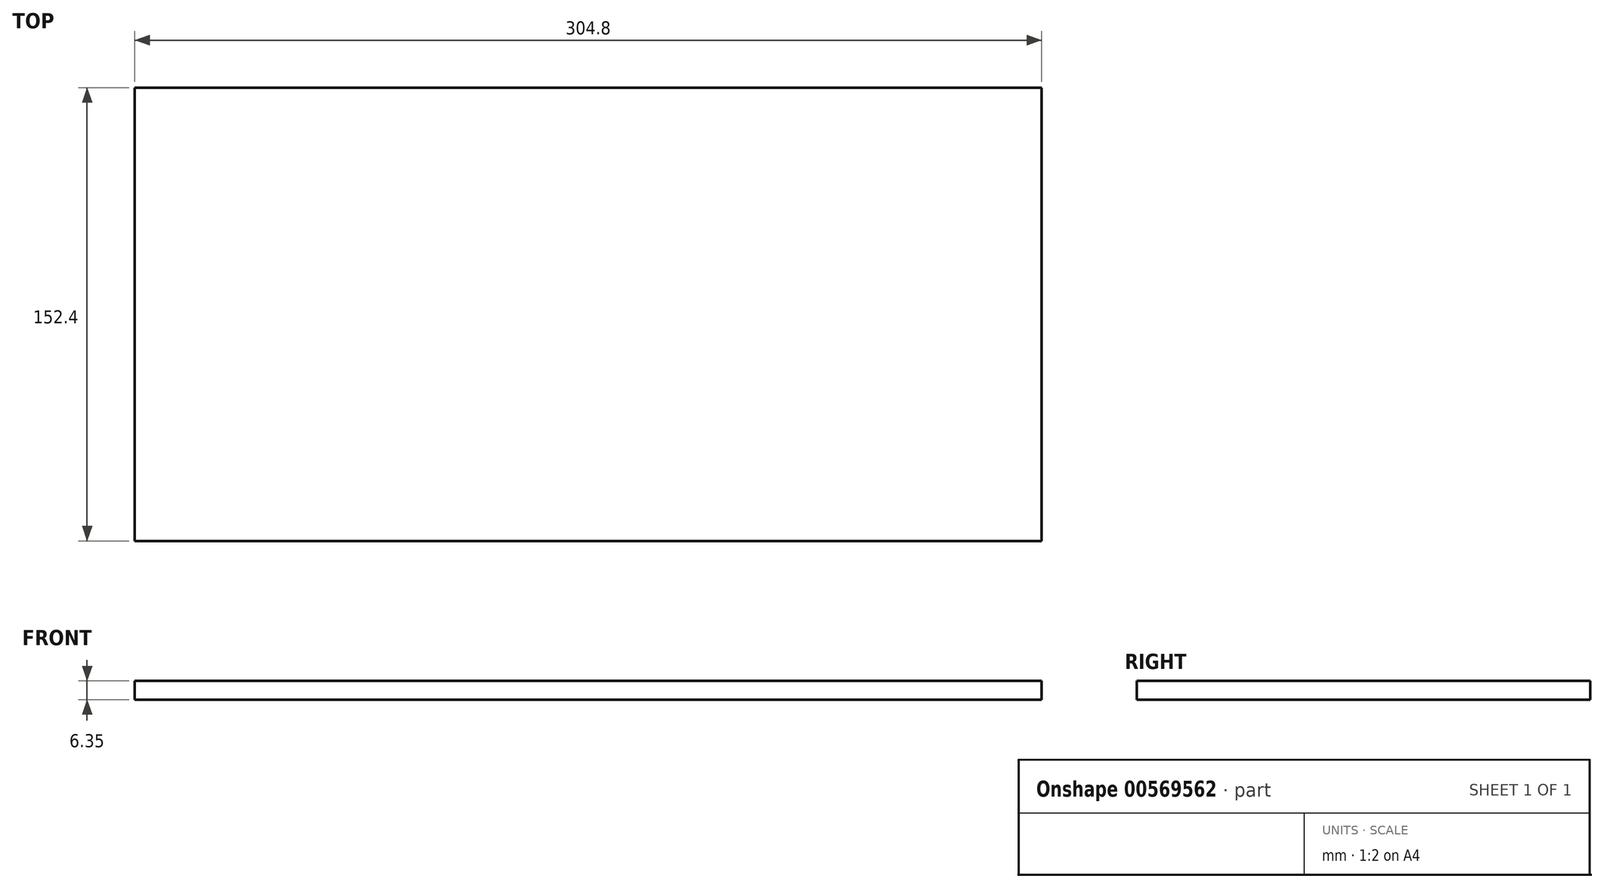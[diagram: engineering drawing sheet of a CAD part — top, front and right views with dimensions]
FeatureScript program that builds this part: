
annotation { "Feature Type Name" : "Feature", "Feature Type Description" : "" }
export const myFeature = defineFeature(function(context is Context, id is Id, definition is map)
    precondition{}
    {
        {
            var Q0;
            Q0=qCreatedBy(makeId("Top.planeOp"),FACE);
            var sketch = newSketch(context, id + "F0", { "sketchPlane" : qUnion([Q0])});
            skLineSegment(sketch, "E0.bottom", {"start": v(152.4, 76.2) * mm, "end": v(-152.4, 76.2) * mm});
            skLineSegment(sketch, "E0.top", {"start": v(152.4, -76.2) * mm, "end": v(-152.4, -76.2) * mm});
            skLineSegment(sketch, "E0.left", {"start": v(152.4, 76.2) * mm, "end": v(152.4, -76.2) * mm});
            skLineSegment(sketch, "E0.right", {"start": v(-152.4, 76.2) * mm, "end": v(-152.4, -76.2) * mm});
            skPoint(sketch, "E0.middle", {"position": v(0, 0) * mm});
            skSolve(sketch);
        }
        {
            var Q0;
            Q0 = qSketchRegion(id + "F0", true);
            extrude(context, id + "F1", {"entities" : qUnion([Q0]), "depth" : 6.35 * mm, "offsetDistance" : 25.4 * mm});
        }
    });
